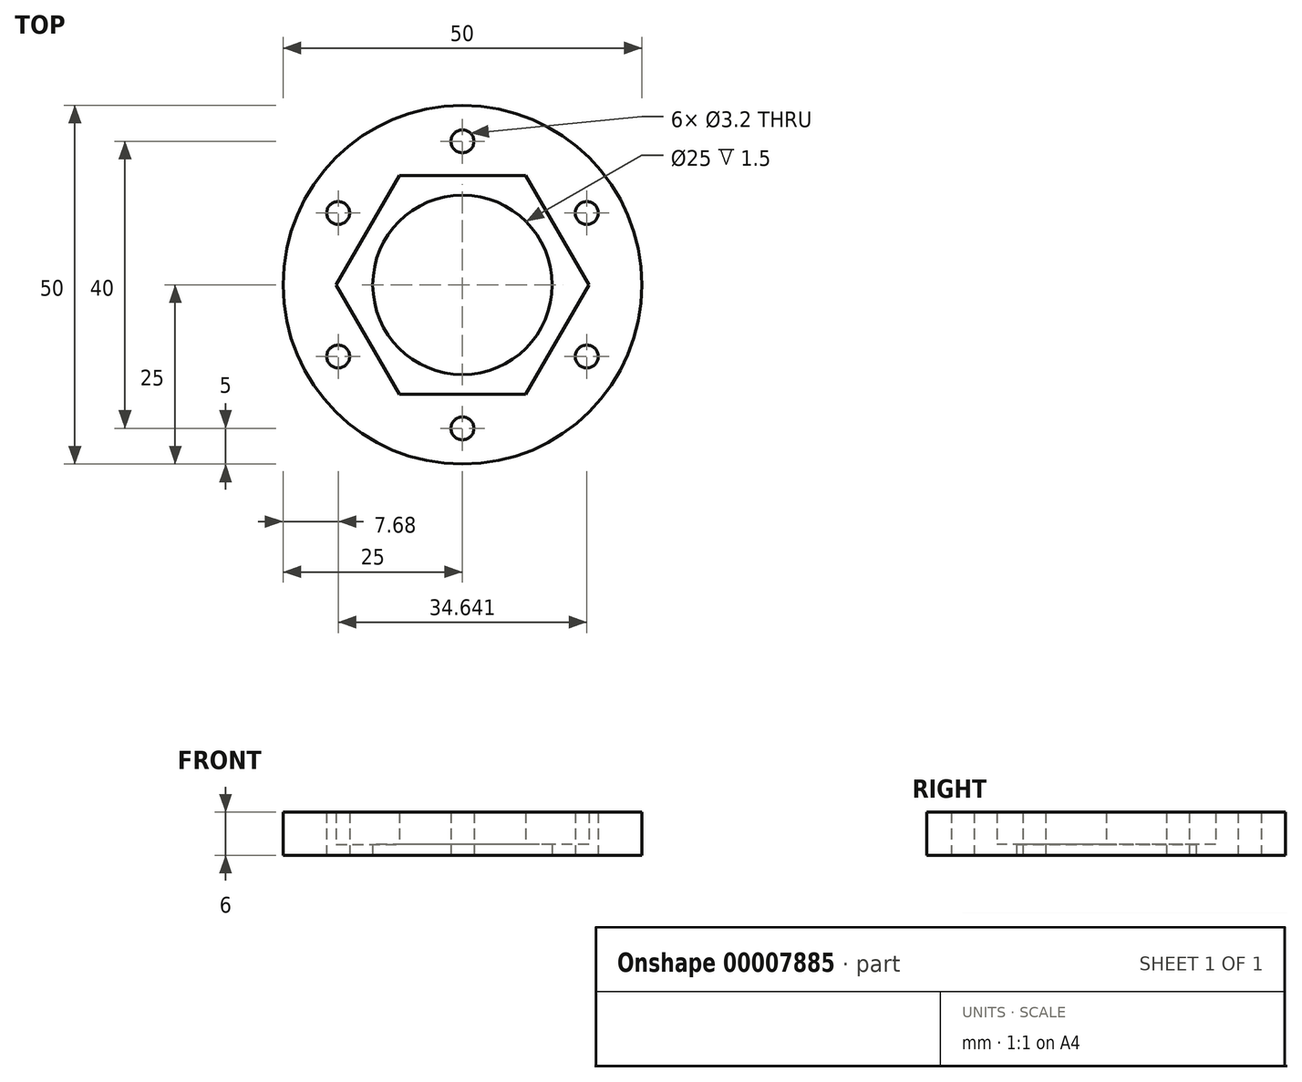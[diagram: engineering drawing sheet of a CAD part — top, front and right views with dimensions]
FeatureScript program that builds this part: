
annotation { "Feature Type Name" : "Feature", "Feature Type Description" : "" }
export const myFeature = defineFeature(function(context is Context, id is Id, definition is map)
    precondition{}
    {
        {
            var Q0;
            Q0=qCreatedBy(makeId("Top.planeOp"),FACE);
            var sketch = newSketch(context, id + "F0", { "sketchPlane" : qUnion([Q0])});
            skCircle(sketch, "E0", {"center": v(0, 0) * mm, "radius": 25 * mm});
            skCircle(sketch, "E1.cCircle", {"center": v(0, 0) * mm, "radius": 15.25 * mm, "construction": true});
            skLineSegment(sketch, "E1.0", {"start": v(-8.8, 15.25) * mm, "end": v(8.8, 15.25) * mm, "construction": true});
            skLineSegment(sketch, "E1.1", {"start": v(8.8, 15.25) * mm, "end": v(17.6, 0) * mm, "construction": true});
            skLineSegment(sketch, "E1.2", {"start": v(17.6, 0) * mm, "end": v(8.8, -15.25) * mm, "construction": true});
            skLineSegment(sketch, "E1.3", {"start": v(8.8, -15.25) * mm, "end": v(-8.8, -15.25) * mm, "construction": true});
            skLineSegment(sketch, "E1.4", {"start": v(-8.8, -15.25) * mm, "end": v(-17.6, 0) * mm, "construction": true});
            skLineSegment(sketch, "E1.5", {"start": v(-17.6, 0) * mm, "end": v(-8.8, 15.25) * mm, "construction": true});
            skPoint(sketch, "E1.0.midPoint", {"position": v(0, 15.25) * mm});
            skCircle(sketch, "E2.cCircle", {"center": v(0, 0) * mm, "radius": 20 * mm, "construction": true});
            skLineSegment(sketch, "E2.0", {"start": v(0, 20) * mm, "end": v(17.32, 10) * mm, "construction": true});
            skLineSegment(sketch, "E2.1", {"start": v(17.32, 10) * mm, "end": v(17.32, -10) * mm, "construction": true});
            skLineSegment(sketch, "E2.2", {"start": v(17.32, -10) * mm, "end": v(0, -20) * mm, "construction": true});
            skLineSegment(sketch, "E2.3", {"start": v(0, -20) * mm, "end": v(-17.32, -10) * mm, "construction": true});
            skLineSegment(sketch, "E2.4", {"start": v(-17.32, -10) * mm, "end": v(-17.32, 10) * mm, "construction": true});
            skLineSegment(sketch, "E2.5", {"start": v(-17.32, 10) * mm, "end": v(0, 20) * mm, "construction": true});
            skCircle(sketch, "E3", {"center": v(0, 20) * mm, "radius": 1.6 * mm});
            skCircle(sketch, "E4.1.0", {"center": v(-17.32, 10) * mm, "radius": 1.6 * mm});
            skCircle(sketch, "E4.2.0", {"center": v(-17.32, -10) * mm, "radius": 1.6 * mm});
            skCircle(sketch, "E5.1.3.0", {"center": v(0, -20) * mm, "radius": 1.6 * mm});
            skCircle(sketch, "E5.1.4.0", {"center": v(17.32, -10) * mm, "radius": 1.6 * mm});
            skCircle(sketch, "E5.1.5.0", {"center": v(17.32, 10) * mm, "radius": 1.6 * mm});
            skCircle(sketch, "E6", {"center": v(0, 0) * mm, "radius": 12.5 * mm});
            skSolve(sketch);
        }
        {
            var Q0;
            Q0=makeQuery(id+"F0.imprint","IMPRINT",FACE,{"disambiguationData":[TD([[makeQuery(id+"F0.imprint","IMPRINT",EDGE,{"derivedFrom":sQuery(id+"F0.wireOp",EDGE,"E0")}),1.0]])]});
            var Q1;
            Q1=sQuery(id+"F0.wireOp",EDGE,"E0");
            extrude(context, id + "F1", {"entities" : qUnion([Q0]), "surfaceEntities" : qUnion([Q1]), "depth" : 1.5 * mm});
        }
        {
            var Q0;
            Q0=makeQuery(id+"F1.opExtrude","CAP_FACE",FACE,{"disambiguationData":[OSD([sQuery(id+"F0.wireOp",EDGE,"E0"),sQuery(id+"F0.wireOp",EDGE,"E3"),sQuery(id+"F0.wireOp",EDGE,"E4.1.0"),sQuery(id+"F0.wireOp",EDGE,"E4.2.0"),sQuery(id+"F0.wireOp",EDGE,"E5.1.3.0"),sQuery(id+"F0.wireOp",EDGE,"E5.1.4.0"),sQuery(id+"F0.wireOp",EDGE,"E5.1.5.0"),sQuery(id+"F0.wireOp",EDGE,"E6")])],"isStart":false});
            var sketch = newSketch(context, id + "F2", { "sketchPlane" : qUnion([Q0])});
            skCircle(sketch, "E7.0", {"center": v(0, 0) * mm, "radius": 25 * mm});
            skCircle(sketch, "E8.1", {"center": v(0, 0) * mm, "radius": 15.25 * mm});
            skLineSegment(sketch, "E8.2", {"start": v(-8.8, 15.25) * mm, "end": v(8.8, 15.25) * mm});
            skLineSegment(sketch, "E8.3", {"start": v(8.8, 15.25) * mm, "end": v(17.6, 0) * mm});
            skLineSegment(sketch, "E8.4", {"start": v(17.6, 0) * mm, "end": v(8.8, -15.25) * mm});
            skLineSegment(sketch, "E8.5", {"start": v(8.8, -15.25) * mm, "end": v(-8.8, -15.25) * mm});
            skLineSegment(sketch, "E8.6", {"start": v(-8.8, -15.25) * mm, "end": v(-17.6, 0) * mm});
            skLineSegment(sketch, "E8.7", {"start": v(-17.6, 0) * mm, "end": v(-8.8, 15.25) * mm});
            skPoint(sketch, "E8.8", {"position": v(0, 15.25) * mm});
            skCircle(sketch, "E8.9", {"center": v(0, 0) * mm, "radius": 20 * mm, "construction": true});
            skLineSegment(sketch, "E8.10", {"start": v(0, 20) * mm, "end": v(17.32, 10) * mm, "construction": true});
            skLineSegment(sketch, "E8.11", {"start": v(17.32, 10) * mm, "end": v(17.32, -10) * mm, "construction": true});
            skLineSegment(sketch, "E8.12", {"start": v(17.32, -10) * mm, "end": v(0, -20) * mm, "construction": true});
            skLineSegment(sketch, "E8.13", {"start": v(0, -20) * mm, "end": v(-17.32, -10) * mm, "construction": true});
            skLineSegment(sketch, "E8.14", {"start": v(-17.32, -10) * mm, "end": v(-17.32, 10) * mm, "construction": true});
            skLineSegment(sketch, "E8.15", {"start": v(-17.32, 10) * mm, "end": v(0, 20) * mm, "construction": true});
            skCircle(sketch, "E8.16", {"center": v(0, 20) * mm, "radius": 1.6 * mm});
            skCircle(sketch, "E8.17", {"center": v(-17.32, 10) * mm, "radius": 1.6 * mm});
            skCircle(sketch, "E8.18", {"center": v(-17.32, -10) * mm, "radius": 1.6 * mm});
            skCircle(sketch, "E8.20", {"center": v(0, -20) * mm, "radius": 1.6 * mm});
            skCircle(sketch, "E8.21", {"center": v(17.32, -10) * mm, "radius": 1.6 * mm});
            skCircle(sketch, "E8.22", {"center": v(17.32, 10) * mm, "radius": 1.6 * mm});
            skCircle(sketch, "E8.23", {"center": v(0, 0) * mm, "radius": 12.5 * mm});
            skCircle(sketch, "E9.cCircle", {"center": v(0, 0) * mm, "radius": 15.25 * mm, "construction": true});
            skSolve(sketch);
        }
        {
            var Q0;
            Q0=makeQuery(id+"F2.imprint","IMPRINT",FACE,{"disambiguationData":[TD([[makeQuery(id+"F2.imprint","IMPRINT",EDGE,{"derivedFrom":sQuery(id+"F2.wireOp",EDGE,"E7.0")}),1.0]])]});
            var Q1;
            Q1=sQuery(id+"F2.wireOp",EDGE,"E8.9");
            var Q2;
            Q2=sQuery(id+"F2.wireOp",EDGE,"E8.12");
            var Q3;
            Q3=sQuery(id+"F2.wireOp",EDGE,"E8.11");
            var Q4;
            Q4=sQuery(id+"F2.wireOp",EDGE,"E8.10");
            var Q5;
            Q5=sQuery(id+"F2.wireOp",EDGE,"E8.15");
            var Q6;
            Q6=sQuery(id+"F2.wireOp",EDGE,"E8.14");
            var Q7;
            Q7=sQuery(id+"F0.wireOp",EDGE,"E2.4");
            var Q8;
            Q8=sQuery(id+"F2.wireOp",EDGE,"E8.13");
            extrude(context, id + "F3", {"entities" : qUnion([Q0]), "operationType" : NewBodyOperationType.ADD, "surfaceEntities" : qUnion([Q1, Q2, Q3, Q4, Q5, Q6, Q7, Q8]), "depth" : 4.5 * mm});
        }
    });
